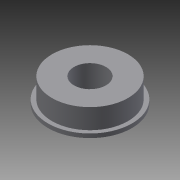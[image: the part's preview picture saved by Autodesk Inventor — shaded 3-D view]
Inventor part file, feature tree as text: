
AUTODESK INVENTOR PART (.ipt)
format: ipt  version: 2014 SP1 (Build 180222100, 222)  size: 88,576 bytes
history: native  units: in
note: dims shown in document units (in); Inventor stores cm internally (conversion verified against a paired STEP export)
features: extrude x2, sketch x2
ambient origin geometry x8: Origin, YZ Plane, XZ Plane, XY Plane, X Axis, Y Axis, Z Axis, Center Point
bodies: Solid1 (feature_tree)
feature tree (4):
  extrude  "Extrusion1"  Depth=0.315in
  extrude  "Extrusion2"  Depth=0.1969in
  sketch  "Sketch1"  dims[d0=0.8268in d1=0.315in]
  sketch  "Sketch2"  dims[d2=0.0394in d3=0.0in d4=0.748in d5=0.1969in d6=0.0in]
